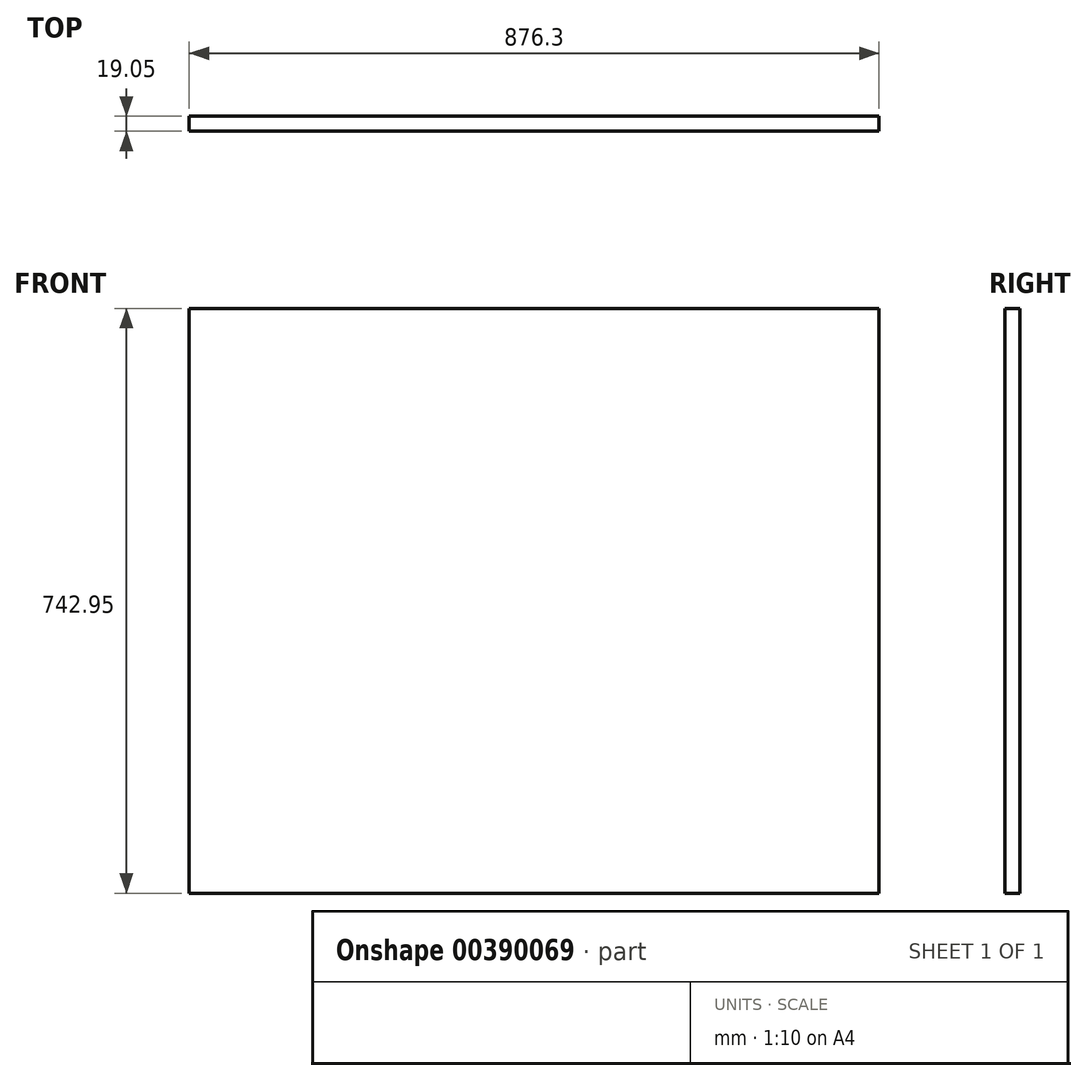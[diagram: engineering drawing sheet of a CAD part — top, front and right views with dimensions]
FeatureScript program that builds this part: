
annotation { "Feature Type Name" : "Feature", "Feature Type Description" : "" }
export const myFeature = defineFeature(function(context is Context, id is Id, definition is map)
    precondition{}
    {
        {
            var Q0;
            Q0=qCreatedBy(makeId("Front.planeOp"),FACE);
            var sketch = newSketch(context, id + "F0", { "sketchPlane" : qUnion([Q0])});
            skLineSegment(sketch, "E0", {"start": v(0, 0) * mm, "end": v(876.3, 0) * mm});
            skLineSegment(sketch, "E1", {"start": v(0, 0) * mm, "end": v(0, 742.95) * mm});
            skLineSegment(sketch, "E2", {"start": v(0, 742.95) * mm, "end": v(876.3, 742.95) * mm});
            skLineSegment(sketch, "E3", {"start": v(876.3, 742.95) * mm, "end": v(876.3, 0) * mm});
            skSolve(sketch);
        }
        {
            var Q0;
            Q0 = qSketchRegion(id + "F0", true);
            extrude(context, id + "F1", {"entities" : qUnion([Q0]), "depth" : 19.05 * mm});
        }
    });
